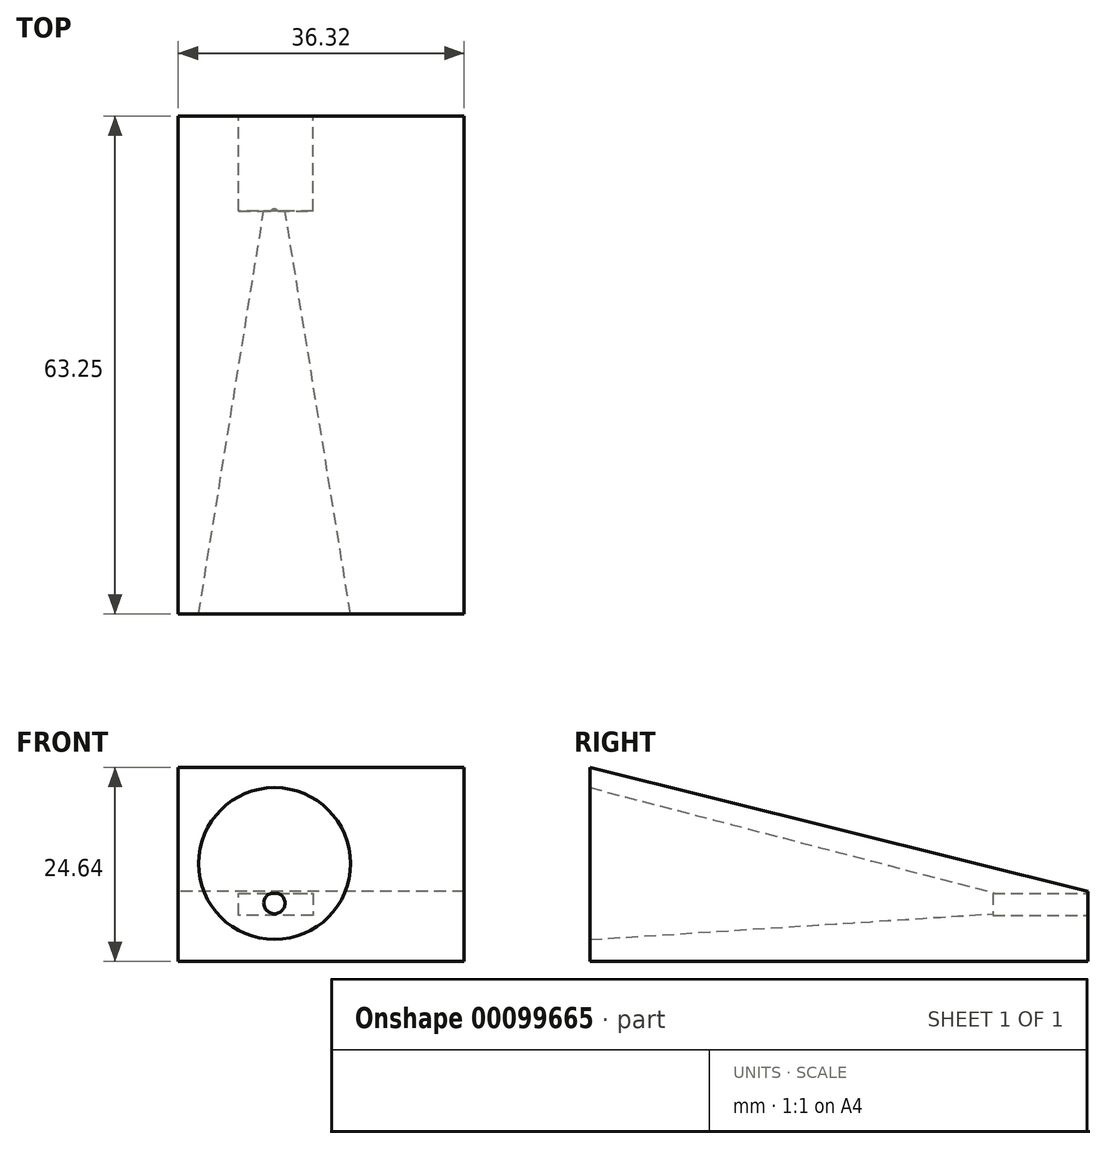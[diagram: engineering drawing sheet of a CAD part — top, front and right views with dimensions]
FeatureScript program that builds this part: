
annotation { "Feature Type Name" : "Feature", "Feature Type Description" : "" }
export const myFeature = defineFeature(function(context is Context, id is Id, definition is map)
    precondition{}
    {
        {
            var Q0;
            Q0=qCreatedBy(makeId("Front.planeOp"),FACE);
            var sketch = newSketch(context, id + "F0", { "sketchPlane" : qUnion([Q0])});
            skLineSegment(sketch, "E0", {"start": v(0, 0) * mm, "end": v(0, 24.64) * mm});
            skLineSegment(sketch, "E1", {"start": v(0, 24.64) * mm, "end": v(-36.32, 24.64) * mm});
            skLineSegment(sketch, "E2", {"start": v(-36.32, 24.64) * mm, "end": v(-36.32, 0) * mm});
            skLineSegment(sketch, "E3", {"start": v(-36.32, 0) * mm, "end": v(0, 0) * mm});
            skSolve(sketch);
        }
        {
            var Q0;
            Q0=makeQuery(id+"F0.imprint","IMPRINT",FACE,{"disambiguationData":[TD([[makeQuery(id+"F0.imprint","IMPRINT",EDGE,{"derivedFrom":sQuery(id+"F0.wireOp",EDGE,"E0")}),1.0]])]});
            extrude(context, id + "F1", {"entities" : qUnion([Q0]), "oppositeDirection" : true, "depth" : 63.25 * mm});
        }
        {
            var Q0;
            Q0=makeQuery(id+"F1.opExtrude","SWEPT_FACE",FACE,{"disambiguationData":[OSD([sQuery(id+"F0.wireOp",EDGE,"E2")])]});
            var sketch = newSketch(context, id + "F2", { "sketchPlane" : qUnion([Q0])});
            skLineSegment(sketch, "E4", {"start": v(0, 24.64) * mm, "end": v(-63.25, 8.9) * mm});
            skSolve(sketch);
        }
        {
            var Q0;
            Q0 = qSketchRegion(id + "F2", true);
            var Q1;
            {var subQ0=sQuery(id+"F2.wireOp",EDGE,"E4");Q1=makeQuery(id+"F2.imprint","IMPRINT",FACE,{"disambiguationData":[TD([[makeQuery(id+"F2.imprint","IMPRINT",EDGE,{"derivedFrom":subQ0}),-1.0]])]});}
            extrude(context, id + "F3", {"entities" : qUnion([Q0, Q1]), "operationType" : NewBodyOperationType.REMOVE, "endBound" : BoundingType.THROUGH_ALL, "oppositeDirection" : true, "depth" : 25.4 * mm});
        }
        {
            var Q0;
            Q0=makeQuery(id+"F1.opExtrude","CAP_FACE",FACE,{"disambiguationData":[OSD([sQuery(id+"F0.wireOp",EDGE,"E0"),sQuery(id+"F0.wireOp",EDGE,"E1"),sQuery(id+"F0.wireOp",EDGE,"E2"),sQuery(id+"F0.wireOp",EDGE,"E3")])],"isStart":true});
            var sketch = newSketch(context, id + "F4", { "sketchPlane" : qUnion([Q0])});
            skPoint(sketch, "E5.endSnap0", {"position": v(-18.16, 24.64) * mm});
            skCircle(sketch, "E6", {"center": v(-24.08, 12.43) * mm, "radius": 9.65 * mm});
            skPoint(sketch, "E7", {"position": v(-24.08, 22.08) * mm});
            skSolve(sketch);
        }
        {
            var Q0;
            Q0=makeQuery(id+"F1.opExtrude","CAP_FACE",FACE,{"disambiguationData":[OSD([sQuery(id+"F0.wireOp",EDGE,"E0"),sQuery(id+"F0.wireOp",EDGE,"E1"),sQuery(id+"F0.wireOp",EDGE,"E2"),sQuery(id+"F0.wireOp",EDGE,"E3")])],"isStart":false});
            var sketch = newSketch(context, id + "F5", { "sketchPlane" : qUnion([Q0])});
            skSolve(sketch);
        }
        {
            var Q0;
            Q0=makeQuery(id+"F5.imprint","IMPRINT",FACE,{"disambiguationData":[TD([[makeQuery(id+"F5.imprint","IMPRINT",EDGE,{"derivedFrom":makeQuery(id+"F1.opExtrude","CAP_EDGE",EDGE,{"disambiguationData":[OSD([sQuery(id+"F0.wireOp",EDGE,"E3")])],"isStart":false})}),-1.0]])]});
            var sketch = newSketch(context, id + "F6", { "sketchPlane" : qUnion([Q0])});
            skLineSegment(sketch, "E8", {"start": v(19.21, 8.67) * mm, "end": v(19.21, 5.85) * mm});
            skLineSegment(sketch, "E9", {"start": v(19.21, 5.85) * mm, "end": v(28.63, 5.85) * mm});
            skLineSegment(sketch, "E10", {"start": v(28.63, 5.85) * mm, "end": v(28.63, 8.67) * mm});
            skLineSegment(sketch, "E11", {"start": v(28.63, 8.67) * mm, "end": v(19.21, 8.67) * mm});
            skSolve(sketch);
        }
        {
            var Q0;
            Q0=qCreatedBy(makeId("Front.planeOp"),FACE);
            cPlane(context, id + "F7", {"entities" : qUnion([Q0]), "cplaneType" : CPlaneType.OFFSET, "offset" : 51.66 * mm, "oppositeDirection" : true, "width" : 152.4 * mm, "height" : 152.4 * mm});
        }
        {
            var Q0;
            Q0=makeQuery(id+"F6.imprint","IMPRINT",FACE,{"disambiguationData":[TD([[makeQuery(id+"F6.imprint","IMPRINT",EDGE,{"derivedFrom":sQuery(id+"F6.wireOp",EDGE,"E8")}),1.0]])]});
            extrude(context, id + "F8", {"entities" : qUnion([Q0]), "operationType" : NewBodyOperationType.REMOVE, "oppositeDirection" : true, "depth" : 12.07 * mm});
        }
        {
            var Q0;
            Q0=qCreatedBy(id+"F7.planeOp",FACE);
            var sketch = newSketch(context, id + "F9", { "sketchPlane" : qUnion([Q0])});
            skCircle(sketch, "E12", {"center": v(-24.1, 7.35) * mm, "radius": 1.27 * mm});
            skSolve(sketch);
        }
        {
            var Q1;
            Q1=makeQuery(id+"F4.imprint","IMPRINT",FACE,{"disambiguationData":[TD([[makeQuery(id+"F4.imprint","IMPRINT",EDGE,{"derivedFrom":sQuery(id+"F4.wireOp",EDGE,"E6")}),1.0]])]});
            var Q2;
            Q2 = qSketchRegion(id + "F9", true);
            loft(context, id + "F10", {"operationType" : NewBodyOperationType.REMOVE, "sheetProfilesArray" : [{ "sheetProfileEntities" : qUnion([Q1]) }, { "sheetProfileEntities" : qUnion([Q2]) }]});
        }
    });
